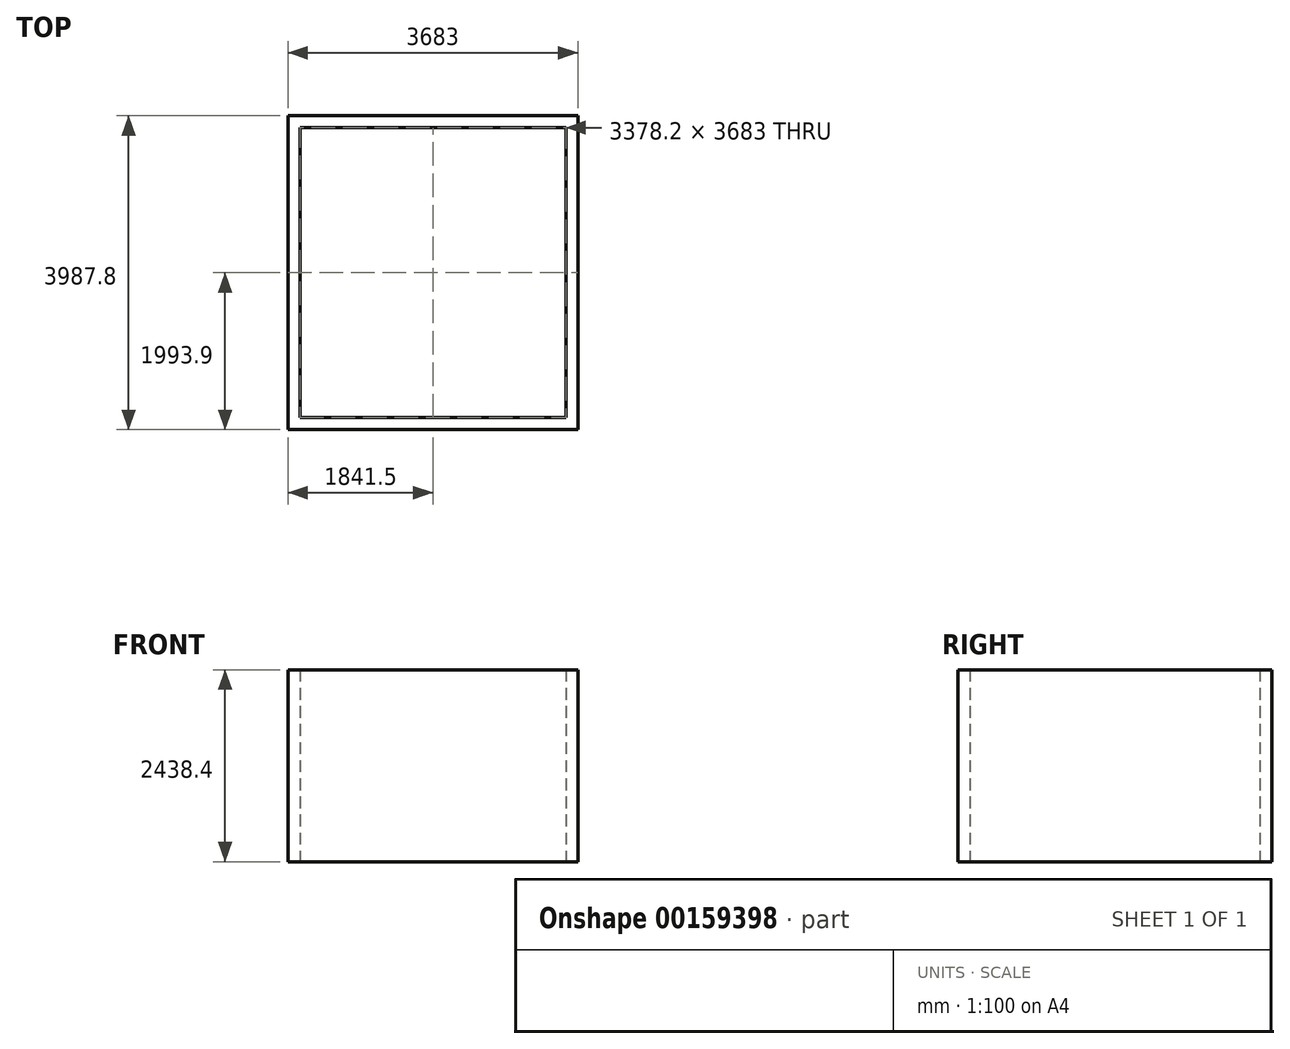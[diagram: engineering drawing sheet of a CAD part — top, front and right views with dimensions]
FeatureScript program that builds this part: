
annotation { "Feature Type Name" : "Feature", "Feature Type Description" : "" }
export const myFeature = defineFeature(function(context is Context, id is Id, definition is map)
    precondition{}
    {
        {
            var Q0;
            Q0=qCreatedBy(makeId("Top.planeOp"),FACE);
            var sketch = newSketch(context, id + "F0", { "sketchPlane" : qUnion([Q0])});
            skLineSegment(sketch, "E0.bottom", {"start": v(-1616.92, 1768.46) * mm, "end": v(1761.28, 1768.46) * mm});
            skLineSegment(sketch, "E0.top", {"start": v(-1616.92, -1914.54) * mm, "end": v(1761.28, -1914.54) * mm});
            skLineSegment(sketch, "E0.left", {"start": v(-1616.92, 1768.46) * mm, "end": v(-1616.92, -1914.54) * mm});
            skLineSegment(sketch, "E0.right", {"start": v(1761.28, 1768.46) * mm, "end": v(1761.28, -1914.54) * mm});
            skLineSegment(sketch, "E1.0", {"start": v(1913.68, 1920.86) * mm, "end": v(1913.68, -2066.94) * mm});
            skLineSegment(sketch, "E1.1", {"start": v(-1769.32, 1920.86) * mm, "end": v(1913.68, 1920.86) * mm});
            skLineSegment(sketch, "E1.2", {"start": v(-1769.32, 1920.86) * mm, "end": v(-1769.32, -2066.94) * mm});
            skLineSegment(sketch, "E1.3", {"start": v(-1769.32, -2066.94) * mm, "end": v(1913.68, -2066.94) * mm});
            skSolve(sketch);
        }
        {
            var Q0;
            Q0 = qSketchRegion(id + "F0", true);
            extrude(context, id + "F1", {"entities" : qUnion([Q0]), "depth" : 2438.4 * mm});
        }
    });
